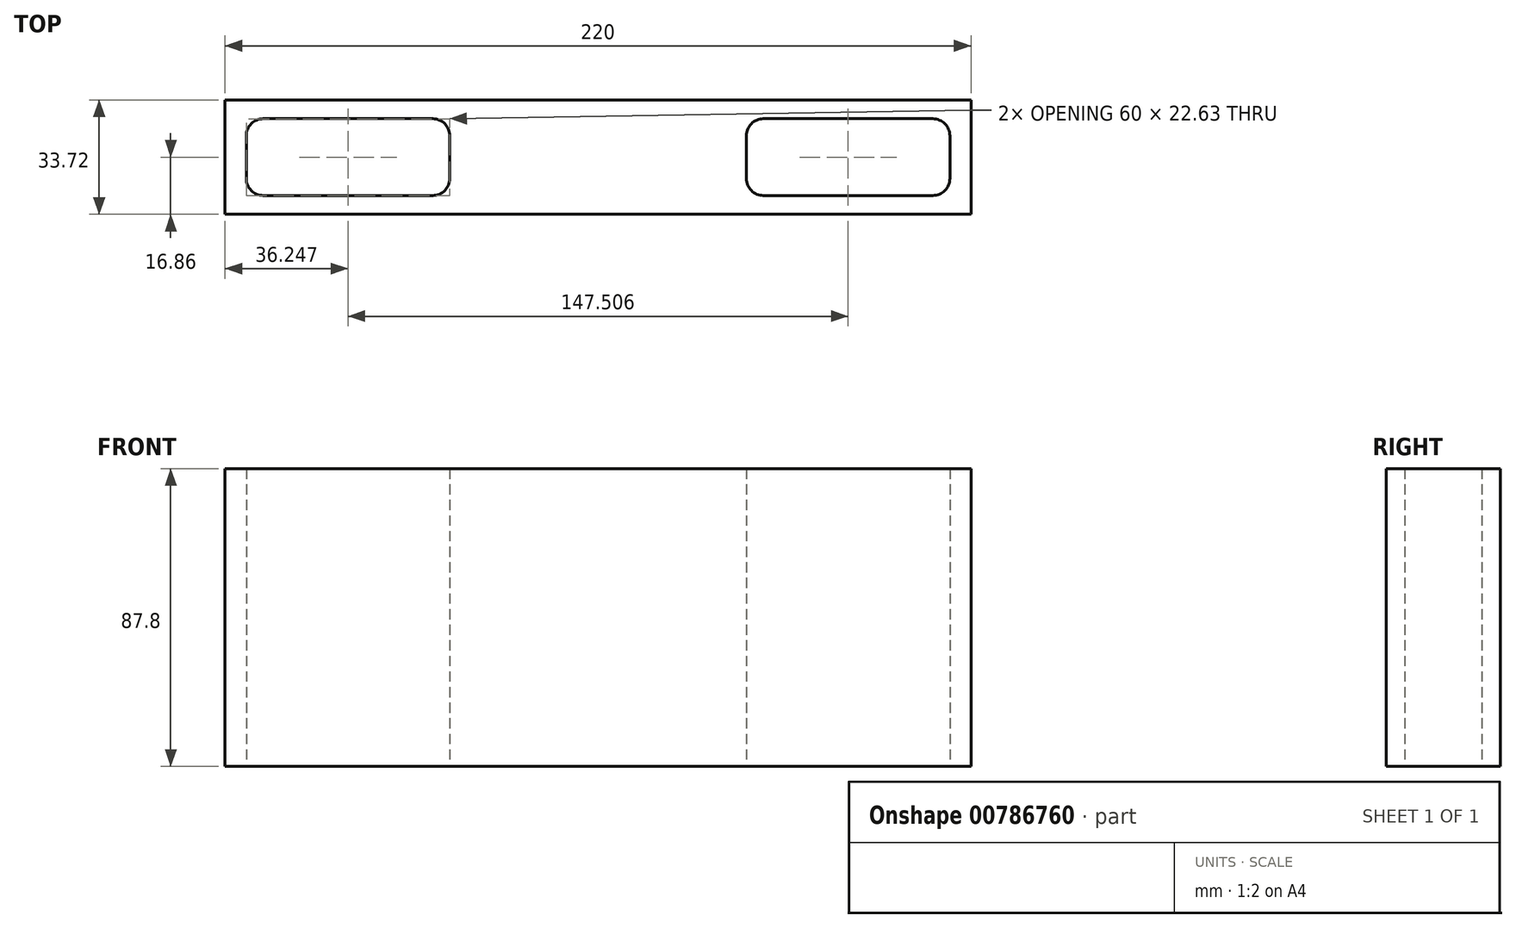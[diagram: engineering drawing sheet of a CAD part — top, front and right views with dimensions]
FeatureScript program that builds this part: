
annotation { "Feature Type Name" : "Feature", "Feature Type Description" : "" }
export const myFeature = defineFeature(function(context is Context, id is Id, definition is map)
    precondition{}
    {
        {
            var Q0;
            Q0=qCreatedBy(makeId("Top.planeOp"),FACE);
            var sketch = newSketch(context, id + "F0", { "sketchPlane" : qUnion([Q0])});
            skLineSegment(sketch, "E0.bottom", {"start": v(110, 16.86) * mm, "end": v(-110, 16.86) * mm});
            skLineSegment(sketch, "E0.top", {"start": v(110, -16.86) * mm, "end": v(-110, -16.86) * mm});
            skLineSegment(sketch, "E0.left", {"start": v(110, 16.86) * mm, "end": v(110, -16.86) * mm});
            skLineSegment(sketch, "E0.right", {"start": v(-110, 16.86) * mm, "end": v(-110, -16.86) * mm});
            skPoint(sketch, "E0.middle", {"position": v(0, 0) * mm});
            skLineSegment(sketch, "E1.bottom", {"start": v(-48.75, 11.32) * mm, "end": v(-98.75, 11.32) * mm});
            skLineSegment(sketch, "E1.top", {"start": v(-48.75, -11.32) * mm, "end": v(-98.75, -11.32) * mm});
            skLineSegment(sketch, "E1.left", {"start": v(103.75, 6.32) * mm, "end": v(103.75, -6.32) * mm});
            skLineSegment(sketch, "E1.right", {"start": v(-103.75, 6.32) * mm, "end": v(-103.75, -6.32) * mm});
            skLineSegment(sketch, "E2", {"start": v(-43.75, 6.32) * mm, "end": v(-43.75, -6.32) * mm});
            skLineSegment(sketch, "E3", {"start": v(43.75, 6.32) * mm, "end": v(43.75, -6.32) * mm});
            skPoint(sketch, "E4.newPointA", {"position": v(103.75, 11.32) * mm});
            skArc(sketch, "E4.filletArc", {"start": v(-43.75, 6.32) * mm, "mid": v(-45.22, 9.85) * mm, "end": v(-48.75, 11.32) * mm});
            skPoint(sketch, "E5.visualSharp", {"position": v(-103.75, 11.32) * mm});
            skArc(sketch, "E5.filletArc", {"start": v(-98.75, 11.32) * mm, "mid": v(-102.29, 9.85) * mm, "end": v(-103.75, 6.32) * mm});
            skLineSegment(sketch, "E6", {"start": v(48.75, 11.32) * mm, "end": v(98.75, 11.32) * mm});
            skPoint(sketch, "E7.visualSharp", {"position": v(43.75, 11.32) * mm});
            skArc(sketch, "E7.filletArc", {"start": v(48.75, 11.32) * mm, "mid": v(45.22, 9.85) * mm, "end": v(43.75, 6.32) * mm});
            skArc(sketch, "E8.filletArc", {"start": v(103.75, 6.32) * mm, "mid": v(102.29, 9.85) * mm, "end": v(98.75, 11.32) * mm});
            skPoint(sketch, "E9.visualSharp", {"position": v(-103.75, -11.32) * mm});
            skArc(sketch, "E9.filletArc", {"start": v(-103.75, -6.32) * mm, "mid": v(-102.29, -9.85) * mm, "end": v(-98.75, -11.32) * mm});
            skPoint(sketch, "E10.newPointB", {"position": v(103.75, -11.32) * mm});
            skArc(sketch, "E10.filletArc", {"start": v(-48.75, -11.32) * mm, "mid": v(-45.22, -9.85) * mm, "end": v(-43.75, -6.32) * mm});
            skLineSegment(sketch, "E11", {"start": v(48.75, -11.32) * mm, "end": v(98.75, -11.32) * mm});
            skArc(sketch, "E12.filletArc", {"start": v(98.75, -11.32) * mm, "mid": v(102.29, -9.85) * mm, "end": v(103.75, -6.32) * mm});
            skPoint(sketch, "E13.visualSharp", {"position": v(43.75, -11.32) * mm});
            skArc(sketch, "E13.filletArc", {"start": v(43.75, -6.32) * mm, "mid": v(45.22, -9.85) * mm, "end": v(48.75, -11.32) * mm});
            skSolve(sketch);
        }
        {
            var Q0;
            Q0=makeQuery(id+"F0.imprint","IMPRINT",FACE,{"disambiguationData":[TD([[makeQuery(id+"F0.imprint","IMPRINT",EDGE,{"derivedFrom":sQuery(id+"F0.wireOp",EDGE,"E0.bottom")}),1.0]])]});
            extrude(context, id + "F1", {"entities" : qUnion([Q0]), "depth" : 87.8 * mm, "offsetDistance" : 25 * mm});
        }
    });
